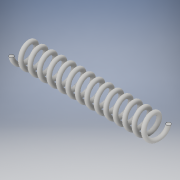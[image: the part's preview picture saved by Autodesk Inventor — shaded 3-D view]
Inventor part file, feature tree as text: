
AUTODESK INVENTOR PART (.ipt)
format: ipt  version: 2018.3 (Build 223284000, 284)  size: 335,872 bytes
history: native  units: in
note: dims shown in document units (in); Inventor stores cm internally (conversion verified against a paired STEP export)
features: helix x1, sketch x1
ambient origin geometry x8: Origin, YZ Plane, XZ Plane, XY Plane, X Axis, Y Axis, Z Axis, Center Point
bodies: Solid1 (feature_tree)
feature tree (2):
  helix  "Coil1"  [1 undecoded]
  sketch  "Sketch1"  dims[d1=0.593in d2=0.593in d3=5.7087in d4=0.0in d5=90.0deg d6=90.0deg d7=0.0in d8=0.0in d9=0.104in d10=0.279in]
note: 1 required parameter value undecoded (feature->parameter linkage not recoverable at this tier; creation-order binding heuristic only, values carry confidence <= 0.55)
